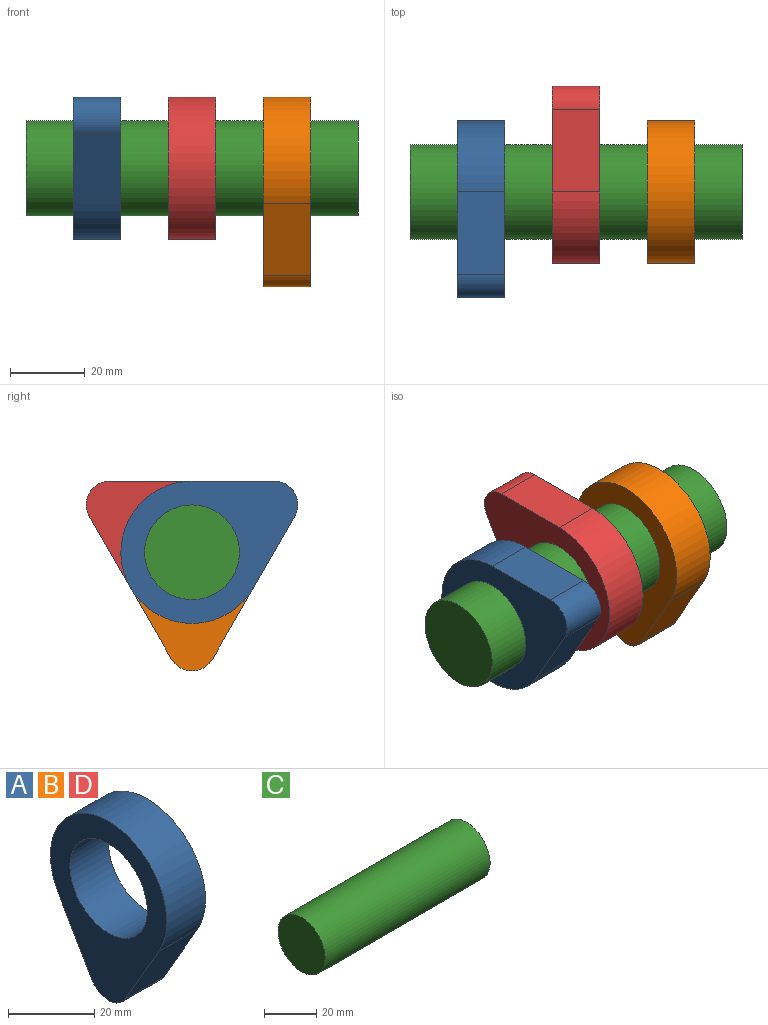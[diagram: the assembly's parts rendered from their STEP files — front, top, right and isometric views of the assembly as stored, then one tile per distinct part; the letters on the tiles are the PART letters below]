
ASSEMBLY  parts=4 mates=5
PART A: 7 faces, bbox 12.7x38.1x50.8 mm
  f0: plane 19.05x12.7mm, normal (0,-0.87,-0.5), area 279.4mm2, adj f1,f4,f5,f6
  f1: cylinder r=6.35mm len=12.7mm, axis (-1,0,0), area 168.9mm2, adj f0,f2,f5,f6
  f2: plane 19.05x12.7mm, normal (0,0.87,-0.5), area 279.4mm2, adj f1,f4,f5,f6
  f3: cylinder r=12.7mm len=25.4mm, axis (-1,0,0), area 1013.4mm2, adj f5,f6
  f4: cylinder r=19.05mm len=38.1mm, axis (-1,0,0), area 1013.4mm2, adj f0,f2,f5,f6
  f5: plane 50.8x38.1mm, normal (1,0,0), area 854.3mm2, adj f0,f1,f2,f3,f4
  f6: plane 50.8x38.1mm, normal (-1,0,0), area 854.3mm2, adj f0,f1,f2,f3,f4
PART B: same geometry as A
PART C: 3 faces, bbox 88.9x25.4x25.4 mm
  f0: cylinder r=12.7mm len=88.9mm, axis (-1,0,0), area 7093.9mm2, adj f1,f2
  f1: plane 25.4x25.4mm, normal (1,0,0), area 506.7mm2, adj f0
  f2: plane 25.4x25.4mm, normal (-1,0,0), area 506.7mm2, adj f0
PART D: same geometry as A
PLACE A rot(axis=(-1,0,0),120deg) t=(-26.34,1.55,-2.36)mm
PLACE B t=(24.46,1.55,-2.36)mm
PLACE C t=(-26.34,1.55,-2.36)mm fixed
PLACE D rot(axis=(1,0,0),120deg) t=(-0.94,1.55,-2.36)mm
MATE planar B.f3 <-> C.f0  axis (-1,0,0) through (37.16,1.55,-2.36)mm
MATE planar D.f3 <-> C.f0  axis (-1,0,0) through (11.76,1.55,-2.36)mm
MATE cylindrical D.f3 <-> C.f0  axis (-1,0,0) through (5.41,1.55,-2.36)mm
MATE cylindrical A.f3 <-> C.f0  axis (-1,0,0) through (-26.34,1.55,-2.36)mm
MATE planar A.f3 <-> C.f0  axis (1,0,0) through (-13.64,1.55,-2.36)mm
